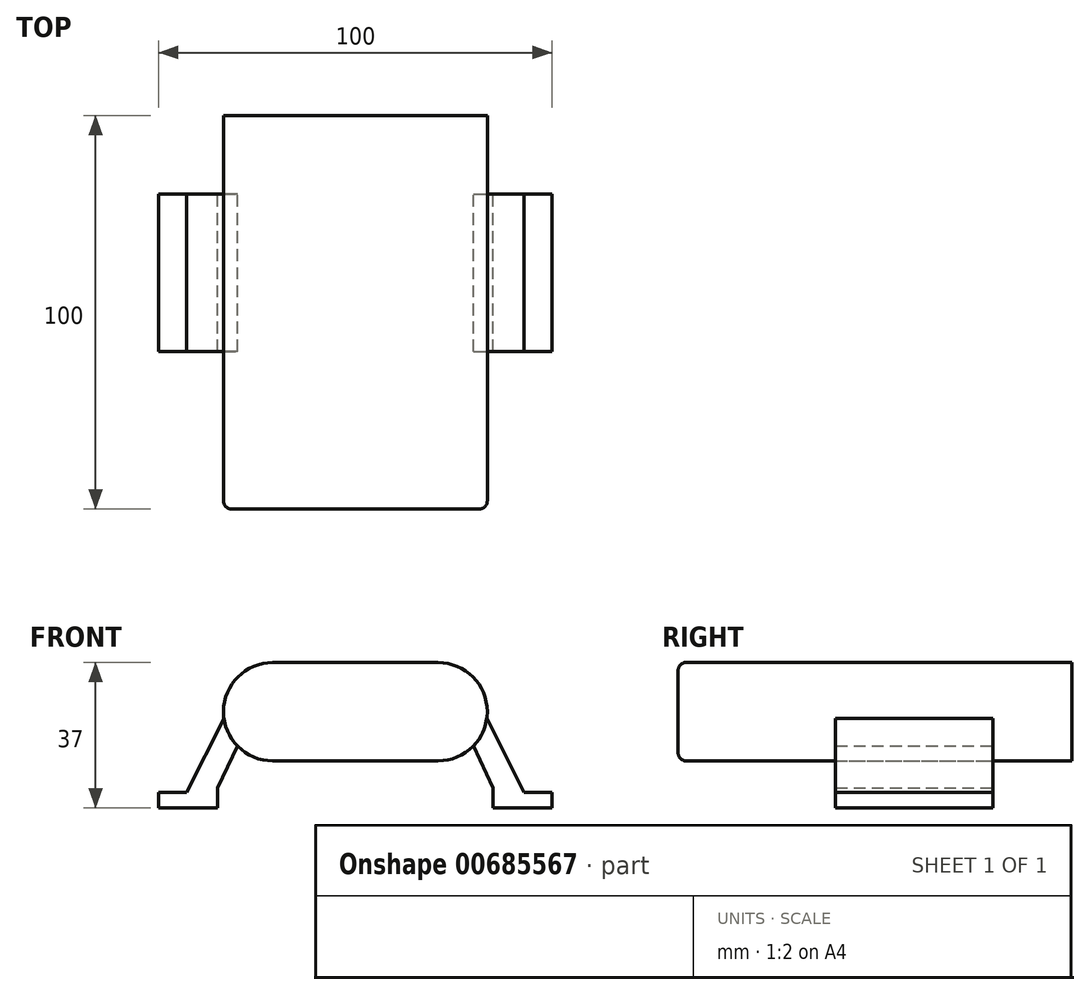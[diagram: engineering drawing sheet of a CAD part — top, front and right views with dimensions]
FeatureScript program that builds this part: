
annotation { "Feature Type Name" : "Feature", "Feature Type Description" : "" }
export const myFeature = defineFeature(function(context is Context, id is Id, definition is map)
    precondition{}
    {
        {
            var Q0;
            Q0=qCreatedBy(makeId("Front.planeOp"),FACE);
            var sketch = newSketch(context, id + "F0", { "sketchPlane" : qUnion([Q0])});
            skLineSegment(sketch, "E0", {"start": v(0, -10.82) * mm, "end": v(21, -10.82) * mm});
            skLineSegment(sketch, "E1", {"start": v(0, 14.18) * mm, "end": v(21, 14.18) * mm});
            skArc(sketch, "E2", {"start": v(21, -10.82) * mm, "mid": v(33.5, 1.68) * mm, "end": v(21, 14.18) * mm});
            skLineSegment(sketch, "E3", {"start": v(33.5, 27.24) * mm, "end": v(33.5, -36.32) * mm, "construction": true});
            skLineSegment(sketch, "E4", {"start": v(30, 26.54) * mm, "end": v(30, -31.69) * mm, "construction": true});
            skLineSegment(sketch, "E5", {"start": v(30, -7) * mm, "end": v(35, -17.67) * mm});
            skLineSegment(sketch, "E6", {"start": v(35, -17.67) * mm, "end": v(35, -22.82) * mm});
            skLineSegment(sketch, "E7", {"start": v(35, -22.82) * mm, "end": v(50, -22.82) * mm});
            skLineSegment(sketch, "E8", {"start": v(50, -22.82) * mm, "end": v(50, -18.82) * mm});
            skLineSegment(sketch, "E9", {"start": v(50, -18.82) * mm, "end": v(42.85, -18.82) * mm});
            skLineSegment(sketch, "E10", {"start": v(42.85, -18.82) * mm, "end": v(33.39, 0) * mm});
            skLineSegment(sketch, "E11.MirrorCS", {"start": v(-50, -22.82) * mm, "end": v(-50, -18.82) * mm});
            skLineSegment(sketch, "E12.MirrorCS", {"start": v(-35, -17.67) * mm, "end": v(-35, -22.82) * mm});
            skLineSegment(sketch, "E13.MirrorCS", {"start": v(0, -10.82) * mm, "end": v(-21, -10.82) * mm});
            skLineSegment(sketch, "E14.MirrorCS", {"start": v(0, 14.18) * mm, "end": v(-21, 14.18) * mm});
            skLineSegment(sketch, "E15.MirrorCS", {"start": v(-42.85, -18.82) * mm, "end": v(-33.39, 0) * mm});
            skArc(sketch, "E16.MirrorCS", {"start": v(-21, -10.82) * mm, "mid": v(-33.5, 1.68) * mm, "end": v(-21, 14.18) * mm});
            skLineSegment(sketch, "E17.MirrorCS", {"start": v(-35, -22.82) * mm, "end": v(-50, -22.82) * mm});
            skLineSegment(sketch, "E18.MirrorCS", {"start": v(-50, -18.82) * mm, "end": v(-42.85, -18.82) * mm});
            skLineSegment(sketch, "E19.MirrorCS", {"start": v(-33.5, 27.24) * mm, "end": v(-33.5, -36.32) * mm, "construction": true});
            skLineSegment(sketch, "E20.MirrorCS", {"start": v(-30, 26.54) * mm, "end": v(-30, -31.69) * mm, "construction": true});
            skLineSegment(sketch, "E21.MirrorCS", {"start": v(-30, -7) * mm, "end": v(-35, -17.67) * mm});
            skSolve(sketch);
        }
        {
            var Q0;
            Q0 = qSketchRegion(id + "F0", true);
            extrude(context, id + "F1", {"entities" : qUnion([Q0]), "depth" : 40 * mm, "offsetDistance" : 25 * mm});
        }
        {
            var Q0;
            Q0=makeQuery(id+"F1.opExtrude","CAP_FACE",FACE,{"disambiguationData":[OSD([sQuery(id+"F0.wireOp",EDGE,"E0"),sQuery(id+"F0.wireOp",EDGE,"E1"),sQuery(id+"F0.wireOp",EDGE,"E2"),sQuery(id+"F0.wireOp",EDGE,"E5"),sQuery(id+"F0.wireOp",EDGE,"E6"),sQuery(id+"F0.wireOp",EDGE,"E7"),sQuery(id+"F0.wireOp",EDGE,"E8"),sQuery(id+"F0.wireOp",EDGE,"E9"),sQuery(id+"F0.wireOp",EDGE,"E10"),sQuery(id+"F0.wireOp",EDGE,"E11.MirrorCS"),sQuery(id+"F0.wireOp",EDGE,"E12.MirrorCS"),sQuery(id+"F0.wireOp",EDGE,"E13.MirrorCS"),sQuery(id+"F0.wireOp",EDGE,"E14.MirrorCS"),sQuery(id+"F0.wireOp",EDGE,"E15.MirrorCS"),sQuery(id+"F0.wireOp",EDGE,"E16.MirrorCS"),sQuery(id+"F0.wireOp",EDGE,"E17.MirrorCS"),sQuery(id+"F0.wireOp",EDGE,"E18.MirrorCS"),sQuery(id+"F0.wireOp",EDGE,"E21.MirrorCS")])],"isStart":false});
            var sketch = newSketch(context, id + "F2", { "sketchPlane" : qUnion([Q0])});
            skLineSegment(sketch, "E22", {"start": v(-21, 14.18) * mm, "end": v(21, 14.18) * mm});
            skArc(sketch, "E23", {"start": v(21, -10.82) * mm, "mid": v(33.5, 1.68) * mm, "end": v(21, 14.18) * mm});
            skLineSegment(sketch, "E24", {"start": v(21, -10.82) * mm, "end": v(-21, -10.82) * mm});
            skArc(sketch, "E25", {"start": v(-21, 14.18) * mm, "mid": v(-33.5, 1.68) * mm, "end": v(-21, -10.82) * mm});
            skSolve(sketch);
        }
        {
            var Q0;
            Q0 = qSketchRegion(id + "F2", true);
            extrude(context, id + "F3", {"entities" : qUnion([Q0]), "operationType" : NewBodyOperationType.ADD, "depth" : 40 * mm, "offsetDistance" : 25 * mm});
        }
        {
            var Q0;
            Q0=makeQuery(id+"F1.opExtrude","CAP_FACE",FACE,{"disambiguationData":[OSD([sQuery(id+"F0.wireOp",EDGE,"E0"),sQuery(id+"F0.wireOp",EDGE,"E1"),sQuery(id+"F0.wireOp",EDGE,"E2"),sQuery(id+"F0.wireOp",EDGE,"E5"),sQuery(id+"F0.wireOp",EDGE,"E6"),sQuery(id+"F0.wireOp",EDGE,"E7"),sQuery(id+"F0.wireOp",EDGE,"E8"),sQuery(id+"F0.wireOp",EDGE,"E9"),sQuery(id+"F0.wireOp",EDGE,"E10"),sQuery(id+"F0.wireOp",EDGE,"E11.MirrorCS"),sQuery(id+"F0.wireOp",EDGE,"E12.MirrorCS"),sQuery(id+"F0.wireOp",EDGE,"E13.MirrorCS"),sQuery(id+"F0.wireOp",EDGE,"E14.MirrorCS"),sQuery(id+"F0.wireOp",EDGE,"E15.MirrorCS"),sQuery(id+"F0.wireOp",EDGE,"E16.MirrorCS"),sQuery(id+"F0.wireOp",EDGE,"E17.MirrorCS"),sQuery(id+"F0.wireOp",EDGE,"E18.MirrorCS"),sQuery(id+"F0.wireOp",EDGE,"E21.MirrorCS")])],"isStart":true});
            var sketch = newSketch(context, id + "F4", { "sketchPlane" : qUnion([Q0])});
            skArc(sketch, "E26", {"start": v(21, -10.82) * mm, "mid": v(33.5, 1.68) * mm, "end": v(21, 14.18) * mm});
            skArc(sketch, "E27", {"start": v(-21, 14.18) * mm, "mid": v(-33.5, 1.68) * mm, "end": v(-21, -10.82) * mm});
            skLineSegment(sketch, "E28", {"start": v(-21, -10.82) * mm, "end": v(21, -10.82) * mm});
            skLineSegment(sketch, "E29", {"start": v(21, 14.18) * mm, "end": v(-21, 14.18) * mm});
            skSolve(sketch);
        }
        {
            var Q0;
            Q0 = qSketchRegion(id + "F4", true);
            var Q1;
            Q1 = qSketchRegion(id + "F2", true);
            extrude(context, id + "F5", {"entities" : qUnion([Q0, Q1]), "operationType" : NewBodyOperationType.ADD, "depth" : 20 * mm, "offsetDistance" : 25 * mm});
        }
        {
            var Q0;
            Q0=makeQuery(id+"F3.opExtrude","CAP_EDGE",EDGE,{"disambiguationData":[OSD([sQuery(id+"F2.wireOp",EDGE,"E22")])],"isStart":false});
            var Q1;
            Q1=makeQuery(id+"F3.opExtrude","CAP_EDGE",EDGE,{"disambiguationData":[OSD([sQuery(id+"F2.wireOp",EDGE,"E23")])],"isStart":false});
            var Q2;
            Q2=makeQuery(id+"F3.opExtrude","CAP_EDGE",EDGE,{"disambiguationData":[OSD([sQuery(id+"F2.wireOp",EDGE,"E24")])],"isStart":false});
            var Q3;
            Q3=makeQuery(id+"F3.opExtrude","CAP_EDGE",EDGE,{"disambiguationData":[OSD([sQuery(id+"F2.wireOp",EDGE,"E25")])],"isStart":false});
            fillet(context, id + "F6", {"entities" : qUnion([Q0, Q1, Q2, Q3]), "radius" : 2 * mm, "tangentPropagation" : true, "allowEdgeOverflow" : false});
        }
    });
